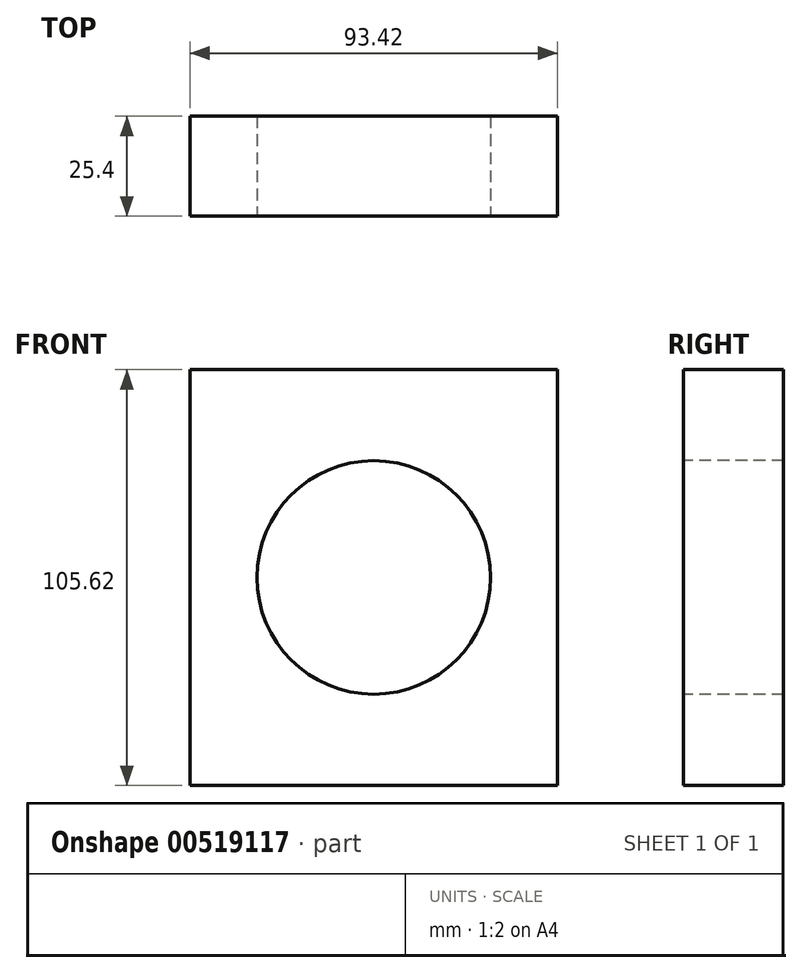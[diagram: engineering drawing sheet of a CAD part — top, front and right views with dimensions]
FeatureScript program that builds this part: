
annotation { "Feature Type Name" : "Feature", "Feature Type Description" : "" }
export const myFeature = defineFeature(function(context is Context, id is Id, definition is map)
    precondition{}
    {
        {
            var Q0;
            Q0=qCreatedBy(makeId("Front.planeOp"),FACE);
            var sketch = newSketch(context, id + "F0", { "sketchPlane" : qUnion([Q0])});
            skLineSegment(sketch, "E0.bottom", {"start": v(-46.7, 52.81) * mm, "end": v(46.7, 52.81) * mm});
            skLineSegment(sketch, "E0.top", {"start": v(-46.7, -52.81) * mm, "end": v(46.7, -52.81) * mm});
            skLineSegment(sketch, "E0.left", {"start": v(-46.7, 52.81) * mm, "end": v(-46.7, -52.81) * mm});
            skLineSegment(sketch, "E0.right", {"start": v(46.7, 52.81) * mm, "end": v(46.7, -52.81) * mm});
            skPoint(sketch, "E0.middle", {"position": v(0, 0) * mm});
            skSolve(sketch);
        }
        {
            var Q0;
            Q0=makeQuery(id+"F0.imprint","IMPRINT",FACE,{"disambiguationData":[TD([[makeQuery(id+"F0.imprint","IMPRINT",EDGE,{"derivedFrom":sQuery(id+"F0.wireOp",EDGE,"E0.bottom")}),-1.0]])]});
            var sketch = newSketch(context, id + "F1", { "sketchPlane" : qUnion([Q0])});
            skCircle(sketch, "E1", {"center": v(0, 0) * mm, "radius": 29.67 * mm});
            skSolve(sketch);
        }
        {
            var Q0;
            Q0=makeQuery(id+"F0.imprint","IMPRINT",FACE,{"disambiguationData":[TD([[makeQuery(id+"F0.imprint","IMPRINT",EDGE,{"derivedFrom":sQuery(id+"F0.wireOp",EDGE,"E0.bottom")}),-1.0]])]});
            var Q1;
            Q1=makeQuery(id+"F1.imprint","IMPRINT",FACE,{"disambiguationData":[TD([[makeQuery(id+"F1.imprint","IMPRINT",EDGE,{"derivedFrom":sQuery(id+"F1.wireOp",EDGE,"E1")}),1.0]])]});
            extrude(context, id + "F2", {"entities" : qUnion([Q0, Q1]), "oppositeDirection" : true, "depth" : 25.4 * mm});
        }
    });
